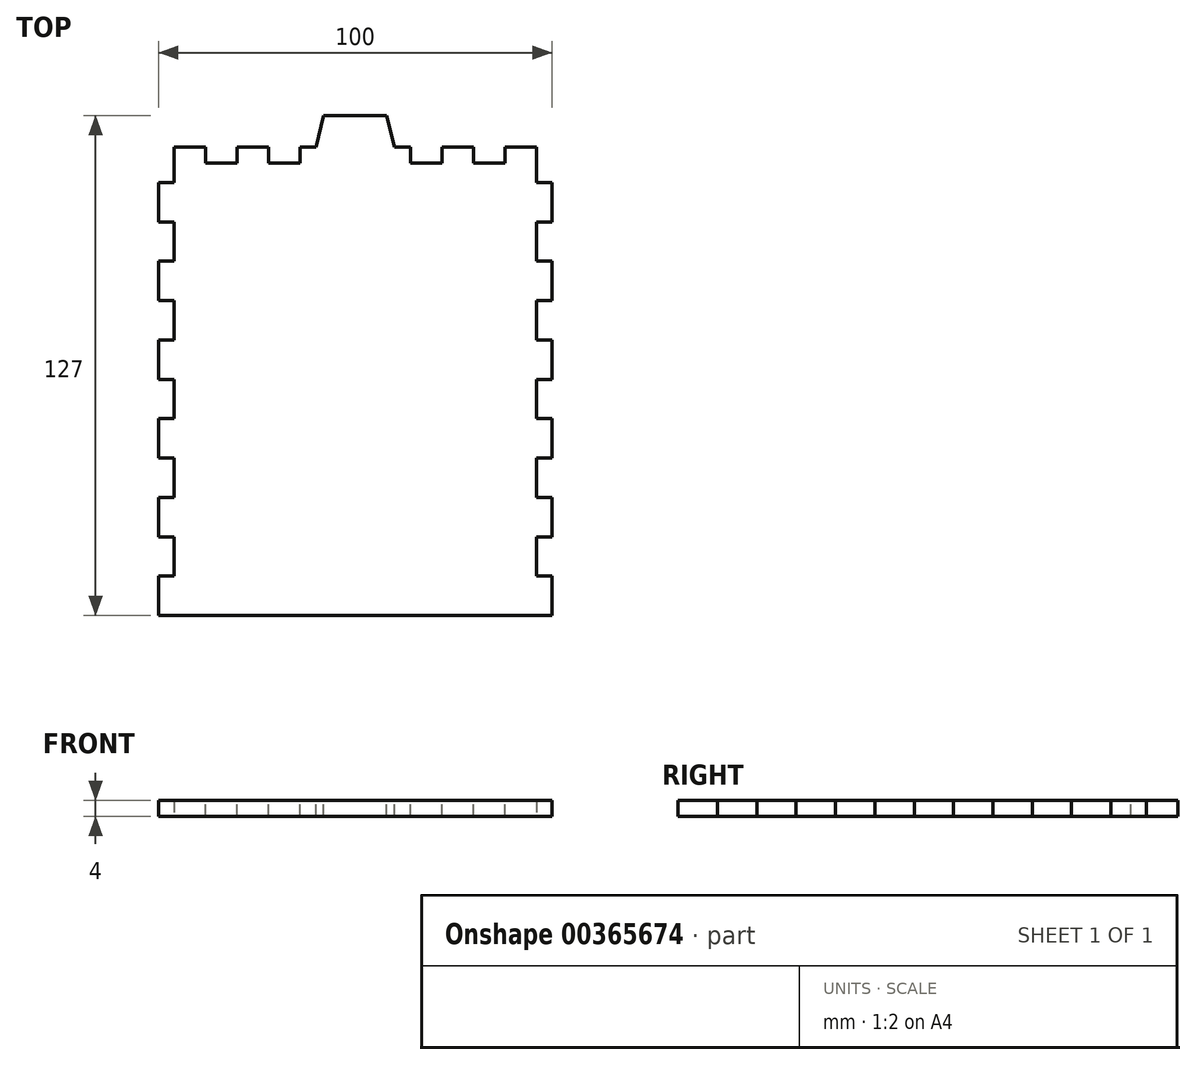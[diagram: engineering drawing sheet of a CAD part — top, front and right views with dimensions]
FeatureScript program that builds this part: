
annotation { "Feature Type Name" : "Feature", "Feature Type Description" : "" }
export const myFeature = defineFeature(function(context is Context, id is Id, definition is map)
    precondition{}
    {
        {
            var Q0;
            Q0=qCreatedBy(makeId("Top.planeOp"),FACE);
            var sketch = newSketch(context, id + "F0", { "sketchPlane" : qUnion([Q0])});
            skLineSegment(sketch, "E0.bottom", {"start": v(0, 0) * mm, "end": v(100, 0) * mm});
            skLineSegment(sketch, "E0.top", {"start": v(0, 119) * mm, "end": v(100, 119) * mm});
            skLineSegment(sketch, "E0.left", {"start": v(0, 0) * mm, "end": v(0, 119) * mm});
            skLineSegment(sketch, "E0.right", {"start": v(100, 0) * mm, "end": v(100, 119) * mm});
            skSolve(sketch);
        }
        {
            var Q0;
            Q0 = qSketchRegion(id + "F0", true);
            extrude(context, id + "F1", {"entities" : qUnion([Q0]), "depth" : 4 * mm});
        }
        {
            var Q0;
            Q0=makeQuery(id+"F1.opExtrude","CAP_FACE",FACE,{"disambiguationData":[OSD([sQuery(id+"F0.wireOp",EDGE,"E0.bottom"),sQuery(id+"F0.wireOp",EDGE,"E0.top"),sQuery(id+"F0.wireOp",EDGE,"E0.left"),sQuery(id+"F0.wireOp",EDGE,"E0.right")])],"isStart":false});
            var sketch = newSketch(context, id + "F2", { "sketchPlane" : qUnion([Q0])});
            skLineSegment(sketch, "E1.bottom", {"start": v(100, 10) * mm, "end": v(96, 10) * mm});
            skLineSegment(sketch, "E1.top", {"start": v(100, 20) * mm, "end": v(96, 20) * mm});
            skLineSegment(sketch, "E1.left", {"start": v(100, 10) * mm, "end": v(100, 20) * mm});
            skLineSegment(sketch, "E1.right", {"start": v(96, 10) * mm, "end": v(96, 20) * mm});
            skLineSegment(sketch, "E2.0.1.0", {"start": v(96, 30) * mm, "end": v(96, 40) * mm});
            skLineSegment(sketch, "E2.0.1.1", {"start": v(100, 30) * mm, "end": v(100, 40) * mm});
            skLineSegment(sketch, "E2.0.1.2", {"start": v(100, 40) * mm, "end": v(96, 40) * mm});
            skLineSegment(sketch, "E2.0.1.3", {"start": v(100, 30) * mm, "end": v(96, 30) * mm});
            skLineSegment(sketch, "E2.0.2.0", {"start": v(96, 50) * mm, "end": v(96, 60) * mm});
            skLineSegment(sketch, "E2.0.2.1", {"start": v(100, 50) * mm, "end": v(100, 60) * mm});
            skLineSegment(sketch, "E2.0.2.2", {"start": v(100, 60) * mm, "end": v(96, 60) * mm});
            skLineSegment(sketch, "E2.0.2.3", {"start": v(100, 50) * mm, "end": v(96, 50) * mm});
            skLineSegment(sketch, "E2.0.3.0", {"start": v(96, 70) * mm, "end": v(96, 80) * mm});
            skLineSegment(sketch, "E2.0.3.1", {"start": v(100, 70) * mm, "end": v(100, 80) * mm});
            skLineSegment(sketch, "E2.0.3.2", {"start": v(100, 80) * mm, "end": v(96, 80) * mm});
            skLineSegment(sketch, "E2.0.3.3", {"start": v(100, 70) * mm, "end": v(96, 70) * mm});
            skLineSegment(sketch, "E2.0.4.0", {"start": v(96, 90) * mm, "end": v(96, 100) * mm});
            skLineSegment(sketch, "E2.0.4.1", {"start": v(100, 90) * mm, "end": v(100, 100) * mm});
            skLineSegment(sketch, "E2.0.4.2", {"start": v(100, 100) * mm, "end": v(96, 100) * mm});
            skLineSegment(sketch, "E2.0.4.3", {"start": v(100, 90) * mm, "end": v(96, 90) * mm});
            skLineSegment(sketch, "E2.0.5.0", {"start": v(96, 110) * mm, "end": v(96, 120) * mm});
            skLineSegment(sketch, "E2.0.5.1", {"start": v(100, 110) * mm, "end": v(100, 120) * mm});
            skLineSegment(sketch, "E2.0.5.2", {"start": v(100, 120) * mm, "end": v(96, 120) * mm});
            skLineSegment(sketch, "E2.0.5.3", {"start": v(100, 110) * mm, "end": v(96, 110) * mm});
            skLineSegment(sketch, "E2.1.0.0", {"start": v(0, 10) * mm, "end": v(0, 20) * mm});
            skLineSegment(sketch, "E2.1.0.1", {"start": v(4, 10) * mm, "end": v(4, 20) * mm});
            skLineSegment(sketch, "E2.1.0.2", {"start": v(4, 20) * mm, "end": v(0, 20) * mm});
            skLineSegment(sketch, "E2.1.0.3", {"start": v(4, 10) * mm, "end": v(0, 10) * mm});
            skLineSegment(sketch, "E2.1.1.0", {"start": v(0, 30) * mm, "end": v(0, 40) * mm});
            skLineSegment(sketch, "E2.1.1.1", {"start": v(4, 30) * mm, "end": v(4, 40) * mm});
            skLineSegment(sketch, "E2.1.1.2", {"start": v(4, 40) * mm, "end": v(0, 40) * mm});
            skLineSegment(sketch, "E2.1.1.3", {"start": v(4, 30) * mm, "end": v(0, 30) * mm});
            skLineSegment(sketch, "E2.1.2.0", {"start": v(0, 50) * mm, "end": v(0, 60) * mm});
            skLineSegment(sketch, "E2.1.2.1", {"start": v(4, 50) * mm, "end": v(4, 60) * mm});
            skLineSegment(sketch, "E2.1.2.2", {"start": v(4, 60) * mm, "end": v(0, 60) * mm});
            skLineSegment(sketch, "E2.1.2.3", {"start": v(4, 50) * mm, "end": v(0, 50) * mm});
            skLineSegment(sketch, "E2.1.3.0", {"start": v(0, 70) * mm, "end": v(0, 80) * mm});
            skLineSegment(sketch, "E2.1.3.1", {"start": v(4, 70) * mm, "end": v(4, 80) * mm});
            skLineSegment(sketch, "E2.1.3.2", {"start": v(4, 80) * mm, "end": v(0, 80) * mm});
            skLineSegment(sketch, "E2.1.3.3", {"start": v(4, 70) * mm, "end": v(0, 70) * mm});
            skLineSegment(sketch, "E2.1.4.0", {"start": v(0, 90) * mm, "end": v(0, 100) * mm});
            skLineSegment(sketch, "E2.1.4.1", {"start": v(4, 90) * mm, "end": v(4, 100) * mm});
            skLineSegment(sketch, "E2.1.4.2", {"start": v(4, 100) * mm, "end": v(0, 100) * mm});
            skLineSegment(sketch, "E2.1.4.3", {"start": v(4, 90) * mm, "end": v(0, 90) * mm});
            skLineSegment(sketch, "E2.1.5.0", {"start": v(0, 110) * mm, "end": v(0, 120) * mm});
            skLineSegment(sketch, "E2.1.5.1", {"start": v(4, 110) * mm, "end": v(4, 120) * mm});
            skLineSegment(sketch, "E2.1.5.2", {"start": v(4, 120) * mm, "end": v(0, 120) * mm});
            skLineSegment(sketch, "E2.1.5.3", {"start": v(4, 110) * mm, "end": v(0, 110) * mm});
            skLineSegment(sketch, "E2.direction1", {"start": v(96, 10) * mm, "end": v(0, 10) * mm, "construction": true});
            skLineSegment(sketch, "E2.direction2", {"start": v(96, 10) * mm, "end": v(96, 30) * mm, "construction": true});
            skLineSegment(sketch, "E3.bottom", {"start": v(12, 119) * mm, "end": v(20, 119) * mm});
            skLineSegment(sketch, "E3.top", {"start": v(12, 115) * mm, "end": v(20, 115) * mm});
            skLineSegment(sketch, "E3.left", {"start": v(12, 119) * mm, "end": v(12, 115) * mm});
            skLineSegment(sketch, "E3.right", {"start": v(20, 119) * mm, "end": v(20, 115) * mm});
            skLineSegment(sketch, "E4.1.0.0", {"start": v(36, 119) * mm, "end": v(36, 115) * mm});
            skLineSegment(sketch, "E4.1.0.1", {"start": v(28, 119) * mm, "end": v(28, 115) * mm});
            skLineSegment(sketch, "E4.1.0.2", {"start": v(28, 115) * mm, "end": v(36, 115) * mm});
            skLineSegment(sketch, "E4.1.0.3", {"start": v(28, 119) * mm, "end": v(36, 119) * mm});
            skLineSegment(sketch, "E4.direction1", {"start": v(12, 115) * mm, "end": v(28, 115) * mm, "construction": true});
            skLineSegment(sketch, "E5", {"start": v(50, 119) * mm, "end": v(50, 0) * mm, "construction": true});
            skLineSegment(sketch, "E6.MirrorCS", {"start": v(88, 115) * mm, "end": v(80, 115) * mm});
            skLineSegment(sketch, "E7.MirrorCS", {"start": v(72, 115) * mm, "end": v(64, 115) * mm});
            skLineSegment(sketch, "E8.MirrorCS", {"start": v(88, 115) * mm, "end": v(72, 115) * mm, "construction": true});
            skLineSegment(sketch, "E9.MirrorCS", {"start": v(72, 119) * mm, "end": v(64, 119) * mm});
            skLineSegment(sketch, "E10.MirrorCS", {"start": v(80, 119) * mm, "end": v(80, 115) * mm});
            skLineSegment(sketch, "E11.MirrorCS", {"start": v(72, 119) * mm, "end": v(72, 115) * mm});
            skLineSegment(sketch, "E12.MirrorCS", {"start": v(88, 119) * mm, "end": v(88, 115) * mm});
            skLineSegment(sketch, "E13.MirrorCS", {"start": v(88, 119) * mm, "end": v(80, 119) * mm});
            skLineSegment(sketch, "E14.MirrorCS", {"start": v(64, 119) * mm, "end": v(64, 115) * mm});
            skSolve(sketch);
        }
        {
            var Q0;
            Q0 = qSketchRegion(id + "F2", true);
            extrude(context, id + "F3", {"entities" : qUnion([Q0]), "operationType" : NewBodyOperationType.REMOVE, "endBound" : BoundingType.THROUGH_ALL, "oppositeDirection" : true, "depth" : 25 * mm});
        }
        {
            var Q0;
            Q0=makeQuery(id+"F1.opExtrude","CAP_FACE",FACE,{"disambiguationData":[OSD([sQuery(id+"F0.wireOp",EDGE,"E0.bottom"),sQuery(id+"F0.wireOp",EDGE,"E0.top"),sQuery(id+"F0.wireOp",EDGE,"E0.left"),sQuery(id+"F0.wireOp",EDGE,"E0.right")])],"isStart":false});
            var sketch = newSketch(context, id + "F4", { "sketchPlane" : qUnion([Q0])});
            skLineSegment(sketch, "E15", {"start": v(40, 119) * mm, "end": v(42, 127) * mm});
            skLineSegment(sketch, "E16", {"start": v(42, 127) * mm, "end": v(58, 127) * mm});
            skLineSegment(sketch, "E17", {"start": v(58, 127) * mm, "end": v(60, 119) * mm});
            skPoint(sketch, "E18", {"position": v(50, 127) * mm});
            skLineSegment(sketch, "E19", {"start": v(50, 127) * mm, "end": v(50, 0) * mm, "construction": true});
            skLineSegment(sketch, "E20", {"start": v(40, 119) * mm, "end": v(60, 119) * mm});
            skSolve(sketch);
        }
        {
            var Q0;
            Q0 = qSketchRegion(id + "F4", true);
            extrude(context, id + "F5", {"entities" : qUnion([Q0]), "operationType" : NewBodyOperationType.ADD, "oppositeDirection" : true, "depth" : 4 * mm});
        }
    });
